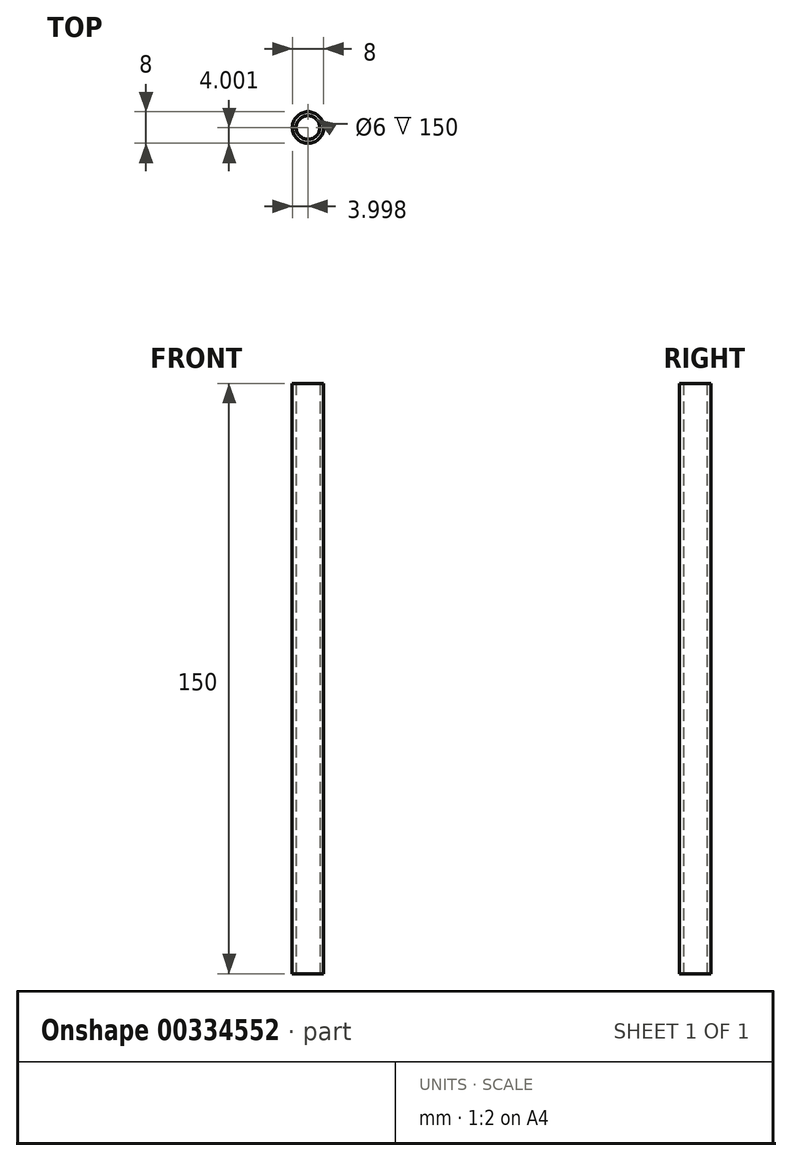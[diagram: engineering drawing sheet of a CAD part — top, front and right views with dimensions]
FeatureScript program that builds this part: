
annotation { "Feature Type Name" : "Feature", "Feature Type Description" : "" }
export const myFeature = defineFeature(function(context is Context, id is Id, definition is map)
    precondition{}
    {
        {
            var Q0;
            Q0=qCreatedBy(makeId("Top.planeOp"),FACE);
            var sketch = newSketch(context, id + "F0", { "sketchPlane" : qUnion([Q0])});
            skCircle(sketch, "E0", {"center": v(-57.46, -45.5) * mm, "radius": 4 * mm});
            skCircle(sketch, "E1", {"center": v(-57.46, -45.5) * mm, "radius": 3 * mm});
            skSolve(sketch);
        }
        {
            var Q0;
            Q0 = qSketchRegion(id + "F0", true);
            extrude(context, id + "F1", {"entities" : qUnion([Q0]), "depth" : 150 * mm});
        }
    });
